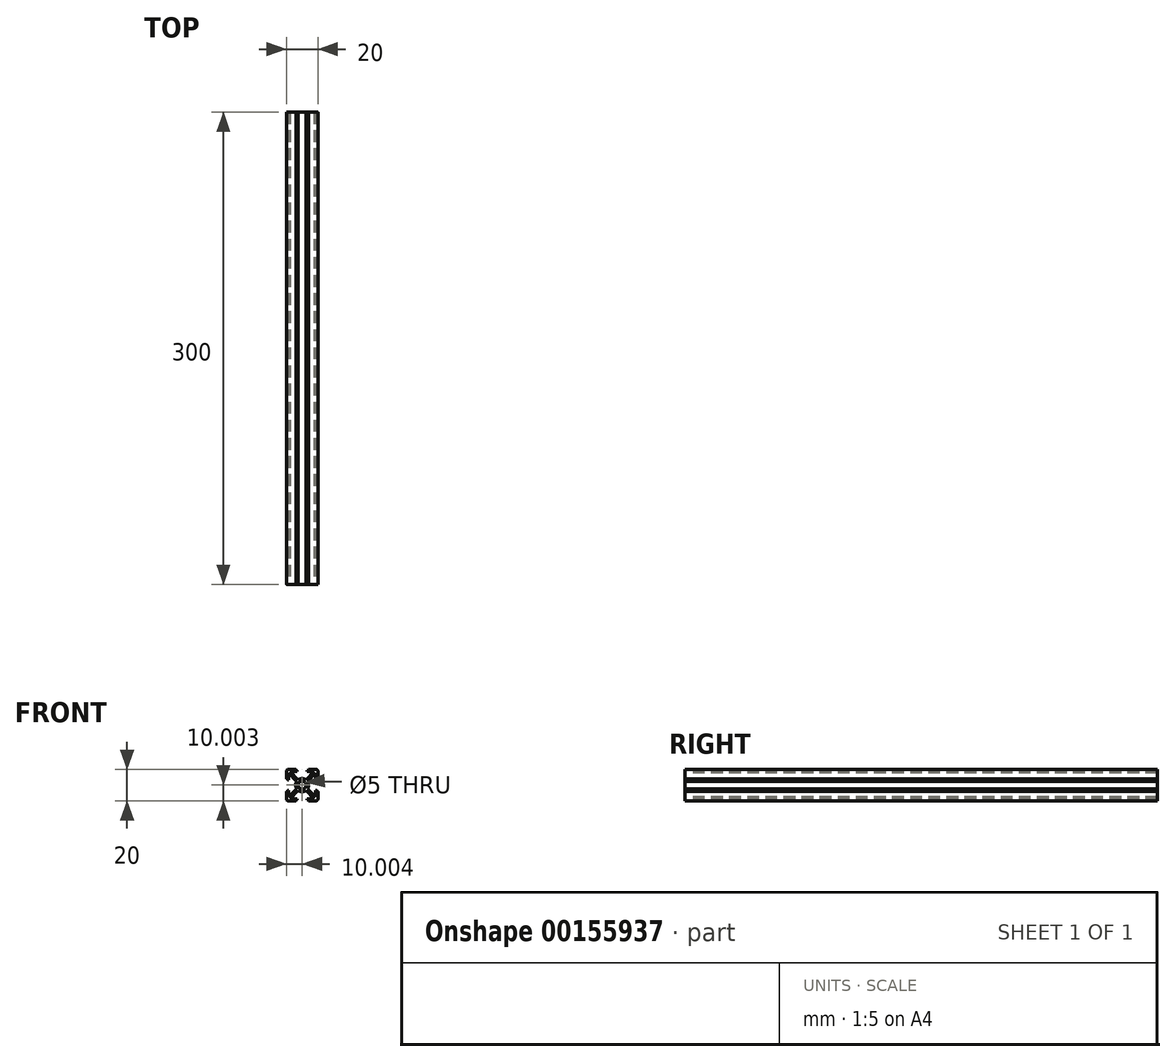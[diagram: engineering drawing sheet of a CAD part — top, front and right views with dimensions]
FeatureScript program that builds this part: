
annotation { "Feature Type Name" : "Feature", "Feature Type Description" : "" }
export const myFeature = defineFeature(function(context is Context, id is Id, definition is map)
    precondition{}
    {
        {
            var Q0;
            Q0=qCreatedBy(makeId("Front.planeOp"),FACE);
            var sketch = newSketch(context, id + "F0", { "sketchPlane" : qUnion([Q0])});
            skArc(sketch, "E0", {"start": v(-44.98, 42.64) * mm, "mid": v(-45.76, 40.2) * mm, "end": v(-44.98, 37.77) * mm});
            skCircle(sketch, "E1", {"center": v(-41.56, 40.2) * mm, "radius": 2.5 * mm});
            skLineSegment(sketch, "E2", {"start": v(-54.61, 53.26) * mm, "end": v(-41.56, 40.2) * mm, "construction": true});
            skLineSegment(sketch, "E3", {"start": v(-41.56, 40.2) * mm, "end": v(-28.67, 27.32) * mm, "construction": true});
            skLineSegment(sketch, "E4", {"start": v(-41.56, 40.2) * mm, "end": v(-29.82, 51.94) * mm, "construction": true});
            skLineSegment(sketch, "E5", {"start": v(-41.56, 40.2) * mm, "end": v(-53.14, 28.61) * mm, "construction": true});
            skLineSegment(sketch, "E6", {"start": v(-55.54, 40.2) * mm, "end": v(-21.72, 40.2) * mm, "construction": true});
            skLineSegment(sketch, "E7", {"start": v(-41.56, 50.17) * mm, "end": v(-41.56, 24.27) * mm, "construction": true});
            skLineSegment(sketch, "E8", {"start": v(-50.36, 50.2) * mm, "end": v(-45.5, 50.2) * mm});
            skLineSegment(sketch, "E9", {"start": v(-44.76, 49.6) * mm, "end": v(-44.76, 48.8) * mm});
            skLineSegment(sketch, "E10", {"start": v(-49.17, 48.8) * mm, "end": v(-43.99, 43.63) * mm});
            skLineSegment(sketch, "E11", {"start": v(-44.76, 48.8) * mm, "end": v(-49.17, 48.8) * mm});
            skLineSegment(sketch, "E12", {"start": v(-45.5, 50.2) * mm, "end": v(-45.5, 49.6) * mm});
            skLineSegment(sketch, "E13", {"start": v(-45.5, 49.6) * mm, "end": v(-44.76, 49.6) * mm});
            skPoint(sketch, "E14.orphan", {"position": v(-44.76, 50.2) * mm});
            skLineSegment(sketch, "E15.MirrorCS", {"start": v(-50.16, 47.81) * mm, "end": v(-44.98, 42.64) * mm});
            skLineSegment(sketch, "E16.MirrorCS", {"start": v(-50.16, 43.4) * mm, "end": v(-50.16, 47.81) * mm});
            skLineSegment(sketch, "E17.MirrorCS", {"start": v(-50.95, 43.4) * mm, "end": v(-50.16, 43.4) * mm});
            skLineSegment(sketch, "E18.MirrorCS", {"start": v(-50.95, 44.15) * mm, "end": v(-50.95, 43.4) * mm});
            skLineSegment(sketch, "E19.MirrorCS", {"start": v(-51.56, 49) * mm, "end": v(-51.56, 44.15) * mm});
            skLineSegment(sketch, "E20.MirrorCS", {"start": v(-51.56, 44.15) * mm, "end": v(-50.95, 44.15) * mm});
            skLineSegment(sketch, "E21.MirrorCS", {"start": v(-32.96, 47.81) * mm, "end": v(-38.13, 42.64) * mm});
            skLineSegment(sketch, "E22.MirrorCS", {"start": v(-33.95, 48.8) * mm, "end": v(-39.12, 43.63) * mm});
            skLineSegment(sketch, "E23.MirrorCS", {"start": v(-37.6, 49.6) * mm, "end": v(-38.36, 49.6) * mm});
            skLineSegment(sketch, "E24.MirrorCS", {"start": v(-32.16, 44.15) * mm, "end": v(-32.16, 43.4) * mm});
            skLineSegment(sketch, "E25.MirrorCS", {"start": v(-31.56, 44.15) * mm, "end": v(-32.16, 44.15) * mm});
            skLineSegment(sketch, "E26.MirrorCS", {"start": v(-38.36, 49.6) * mm, "end": v(-38.36, 48.8) * mm});
            skLineSegment(sketch, "E27.MirrorCS", {"start": v(-37.6, 50.2) * mm, "end": v(-37.6, 49.6) * mm});
            skLineSegment(sketch, "E28.MirrorCS", {"start": v(-32.16, 43.4) * mm, "end": v(-32.96, 43.4) * mm});
            skLineSegment(sketch, "E29.MirrorCS", {"start": v(-32.96, 43.4) * mm, "end": v(-32.96, 47.81) * mm});
            skPoint(sketch, "E30.MirrorP", {"position": v(-38.36, 50.2) * mm});
            skLineSegment(sketch, "E31.MirrorCS", {"start": v(-38.36, 48.8) * mm, "end": v(-33.95, 48.8) * mm});
            skLineSegment(sketch, "E32.MirrorCS", {"start": v(-32.76, 50.2) * mm, "end": v(-37.6, 50.2) * mm});
            skLineSegment(sketch, "E33.MirrorCS", {"start": v(-31.56, 49) * mm, "end": v(-31.56, 44.15) * mm});
            skLineSegment(sketch, "E34.MirrorCS", {"start": v(-32.16, 37) * mm, "end": v(-32.96, 37) * mm});
            skLineSegment(sketch, "E35.MirrorCS", {"start": v(-38.36, 30.8) * mm, "end": v(-38.36, 31.6) * mm});
            skLineSegment(sketch, "E36.MirrorCS", {"start": v(-32.16, 36.25) * mm, "end": v(-32.16, 37) * mm});
            skLineSegment(sketch, "E37.MirrorCS", {"start": v(-37.6, 30.8) * mm, "end": v(-38.36, 30.8) * mm});
            skLineSegment(sketch, "E38.MirrorCS", {"start": v(-31.56, 36.25) * mm, "end": v(-32.16, 36.25) * mm});
            skLineSegment(sketch, "E39.MirrorCS", {"start": v(-37.6, 30.2) * mm, "end": v(-37.6, 30.8) * mm});
            skLineSegment(sketch, "E40.MirrorCS", {"start": v(-32.76, 30.2) * mm, "end": v(-37.6, 30.2) * mm});
            skLineSegment(sketch, "E41.MirrorCS", {"start": v(-31.56, 31.4) * mm, "end": v(-31.56, 36.25) * mm});
            skLineSegment(sketch, "E42.MirrorCS", {"start": v(-33.95, 31.6) * mm, "end": v(-39.12, 36.78) * mm});
            skLineSegment(sketch, "E43.MirrorCS", {"start": v(-32.96, 37) * mm, "end": v(-32.96, 32.6) * mm});
            skPoint(sketch, "E44.MirrorP", {"position": v(-38.36, 30.2) * mm});
            skLineSegment(sketch, "E45.MirrorCS", {"start": v(-38.36, 31.6) * mm, "end": v(-33.95, 31.6) * mm});
            skLineSegment(sketch, "E46.MirrorCS", {"start": v(-32.96, 32.6) * mm, "end": v(-38.13, 37.77) * mm});
            skLineSegment(sketch, "E47.MirrorCS", {"start": v(-45.5, 30.8) * mm, "end": v(-44.76, 30.8) * mm});
            skLineSegment(sketch, "E48.MirrorCS", {"start": v(-51.56, 36.25) * mm, "end": v(-50.95, 36.25) * mm});
            skLineSegment(sketch, "E49.MirrorCS", {"start": v(-50.95, 36.25) * mm, "end": v(-50.95, 37) * mm});
            skLineSegment(sketch, "E50.MirrorCS", {"start": v(-50.95, 37) * mm, "end": v(-50.16, 37) * mm});
            skLineSegment(sketch, "E51.MirrorCS", {"start": v(-45.5, 30.2) * mm, "end": v(-45.5, 30.8) * mm});
            skLineSegment(sketch, "E52.MirrorCS", {"start": v(-44.76, 30.8) * mm, "end": v(-44.76, 31.6) * mm});
            skLineSegment(sketch, "E53.MirrorCS", {"start": v(-50.16, 37) * mm, "end": v(-50.16, 32.6) * mm});
            skLineSegment(sketch, "E54.MirrorCS", {"start": v(-50.16, 32.6) * mm, "end": v(-44.98, 37.77) * mm});
            skLineSegment(sketch, "E55.MirrorCS", {"start": v(-50.36, 30.2) * mm, "end": v(-45.5, 30.2) * mm});
            skPoint(sketch, "E56.MirrorP", {"position": v(-44.76, 30.2) * mm});
            skLineSegment(sketch, "E57.MirrorCS", {"start": v(-51.56, 31.4) * mm, "end": v(-51.56, 36.25) * mm});
            skLineSegment(sketch, "E58.MirrorCS", {"start": v(-49.17, 31.6) * mm, "end": v(-43.99, 36.78) * mm});
            skLineSegment(sketch, "E59.MirrorCS", {"start": v(-44.76, 31.6) * mm, "end": v(-49.17, 31.6) * mm});
            skPoint(sketch, "E60.visualSharp", {"position": v(-51.56, 50.2) * mm});
            skArc(sketch, "E60.filletArc", {"start": v(-50.36, 50.2) * mm, "mid": v(-51.2, 49.85) * mm, "end": v(-51.56, 49) * mm});
            skPoint(sketch, "E61.visualSharp", {"position": v(-31.56, 50.2) * mm});
            skArc(sketch, "E61.filletArc", {"start": v(-31.56, 49) * mm, "mid": v(-31.9, 49.85) * mm, "end": v(-32.76, 50.2) * mm});
            skPoint(sketch, "E62.visualSharp", {"position": v(-31.56, 30.2) * mm});
            skArc(sketch, "E62.filletArc", {"start": v(-32.76, 30.2) * mm, "mid": v(-31.9, 30.55) * mm, "end": v(-31.56, 31.4) * mm});
            skPoint(sketch, "E63.visualSharp", {"position": v(-51.56, 30.2) * mm});
            skArc(sketch, "E63.filletArc", {"start": v(-51.56, 31.4) * mm, "mid": v(-51.2, 30.55) * mm, "end": v(-50.36, 30.2) * mm});
            skArc(sketch, "E64.trimOffspring", {"start": v(-39.12, 43.63) * mm, "mid": v(-41.56, 44.4) * mm, "end": v(-43.99, 43.63) * mm});
            skArc(sketch, "E65.trimOffspring", {"start": v(-43.99, 36.78) * mm, "mid": v(-41.56, 36) * mm, "end": v(-39.12, 36.78) * mm});
            skArc(sketch, "E66.trimOffspring", {"start": v(-38.13, 37.77) * mm, "mid": v(-37.36, 40.2) * mm, "end": v(-38.13, 42.64) * mm});
            skSolve(sketch);
        }
        {
            var Q0;
            Q0=makeQuery(id+"F0.imprint","IMPRINT",FACE,{"disambiguationData":[TD([[makeQuery(id+"F0.imprint","IMPRINT",EDGE,{"derivedFrom":sQuery(id+"F0.wireOp",EDGE,"E0")}),1.0]])]});
            extrude(context, id + "F1", {"entities" : qUnion([Q0]), "oppositeDirection" : true, "depth" : 300 * mm, "offsetDistance" : 25 * mm});
        }
    });
